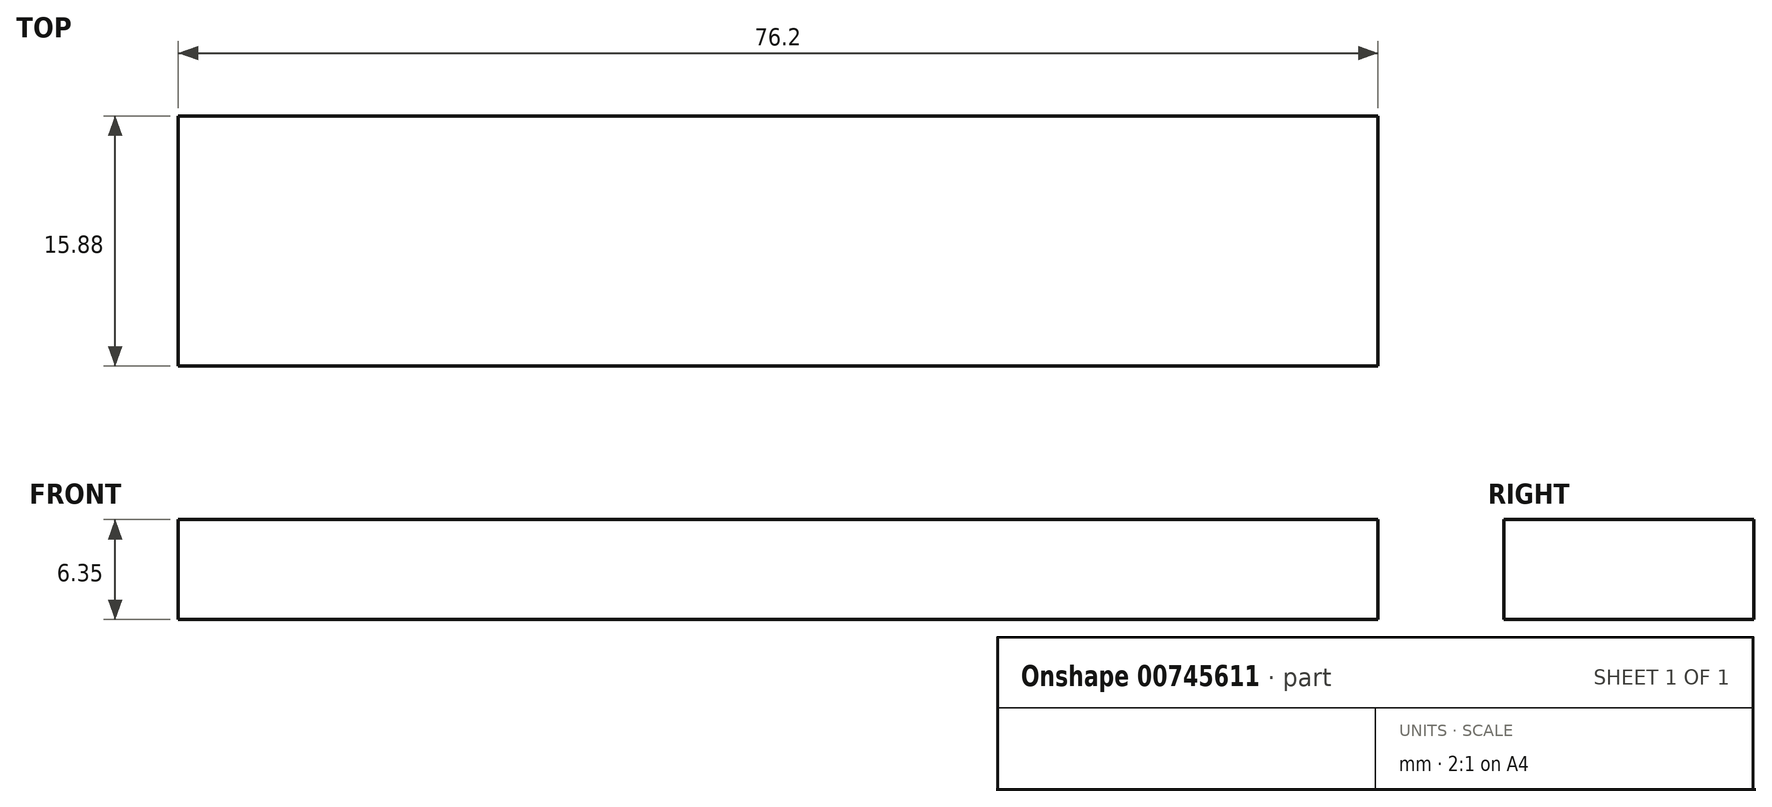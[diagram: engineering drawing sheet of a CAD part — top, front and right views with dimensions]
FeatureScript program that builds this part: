
annotation { "Feature Type Name" : "Feature", "Feature Type Description" : "" }
export const myFeature = defineFeature(function(context is Context, id is Id, definition is map)
    precondition{}
    {
        {
            var Q0;
            Q0=qCreatedBy(makeId("Top.planeOp"),FACE);
            var sketch = newSketch(context, id + "F0", { "sketchPlane" : qUnion([Q0])});
            skLineSegment(sketch, "E0", {"start": v(-48.7, -15.94) * mm, "end": v(-48.7, -31.82) * mm});
            skLineSegment(sketch, "E1", {"start": v(-48.7, -31.82) * mm, "end": v(27.5, -31.82) * mm});
            skLineSegment(sketch, "E2", {"start": v(27.5, -31.82) * mm, "end": v(27.5, -15.94) * mm});
            skLineSegment(sketch, "E3", {"start": v(27.5, -15.94) * mm, "end": v(-48.7, -15.94) * mm});
            skSolve(sketch);
        }
        {
            var Q0;
            Q0 = qSketchRegion(id + "F0", true);
            extrude(context, id + "F1", {"entities" : qUnion([Q0]), "depth" : 6.35 * mm, "offsetDistance" : 25.4 * mm});
        }
    });
